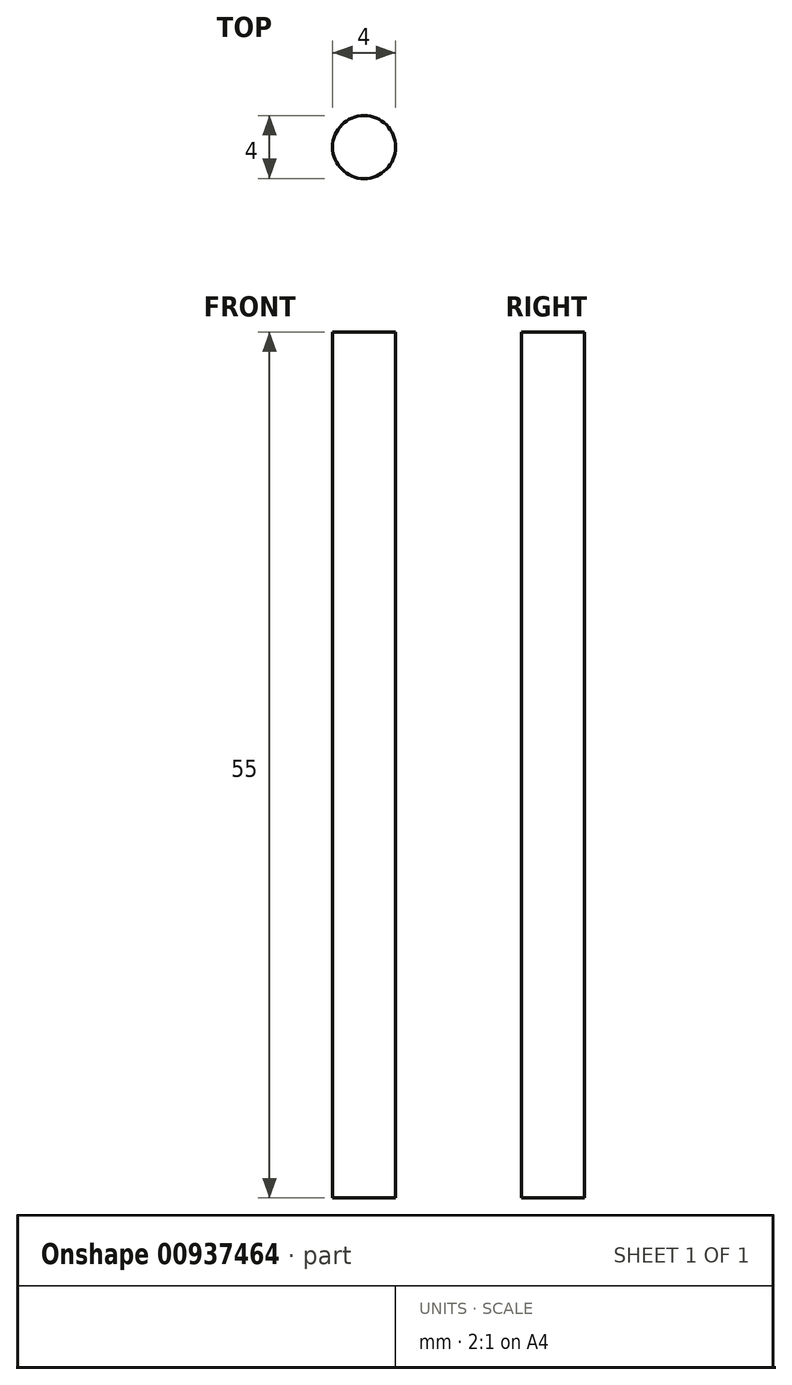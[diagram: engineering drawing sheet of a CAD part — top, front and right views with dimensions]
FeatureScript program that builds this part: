
annotation { "Feature Type Name" : "Feature", "Feature Type Description" : "" }
export const myFeature = defineFeature(function(context is Context, id is Id, definition is map)
    precondition{}
    {
        {
            var Q0;
            Q0=qCreatedBy(makeId("Top.planeOp"),FACE);
            var sketch = newSketch(context, id + "F0", { "sketchPlane" : qUnion([Q0])});
            skCircle(sketch, "E0", {"center": v(0, 0) * mm, "radius": 2 * mm});
            skSolve(sketch);
        }
        {
            var Q0;
            Q0 = qSketchRegion(id + "F0", true);
            extrude(context, id + "F1", {"entities" : qUnion([Q0]), "depth" : 55 * mm, "offsetDistance" : 25 * mm});
        }
    });
